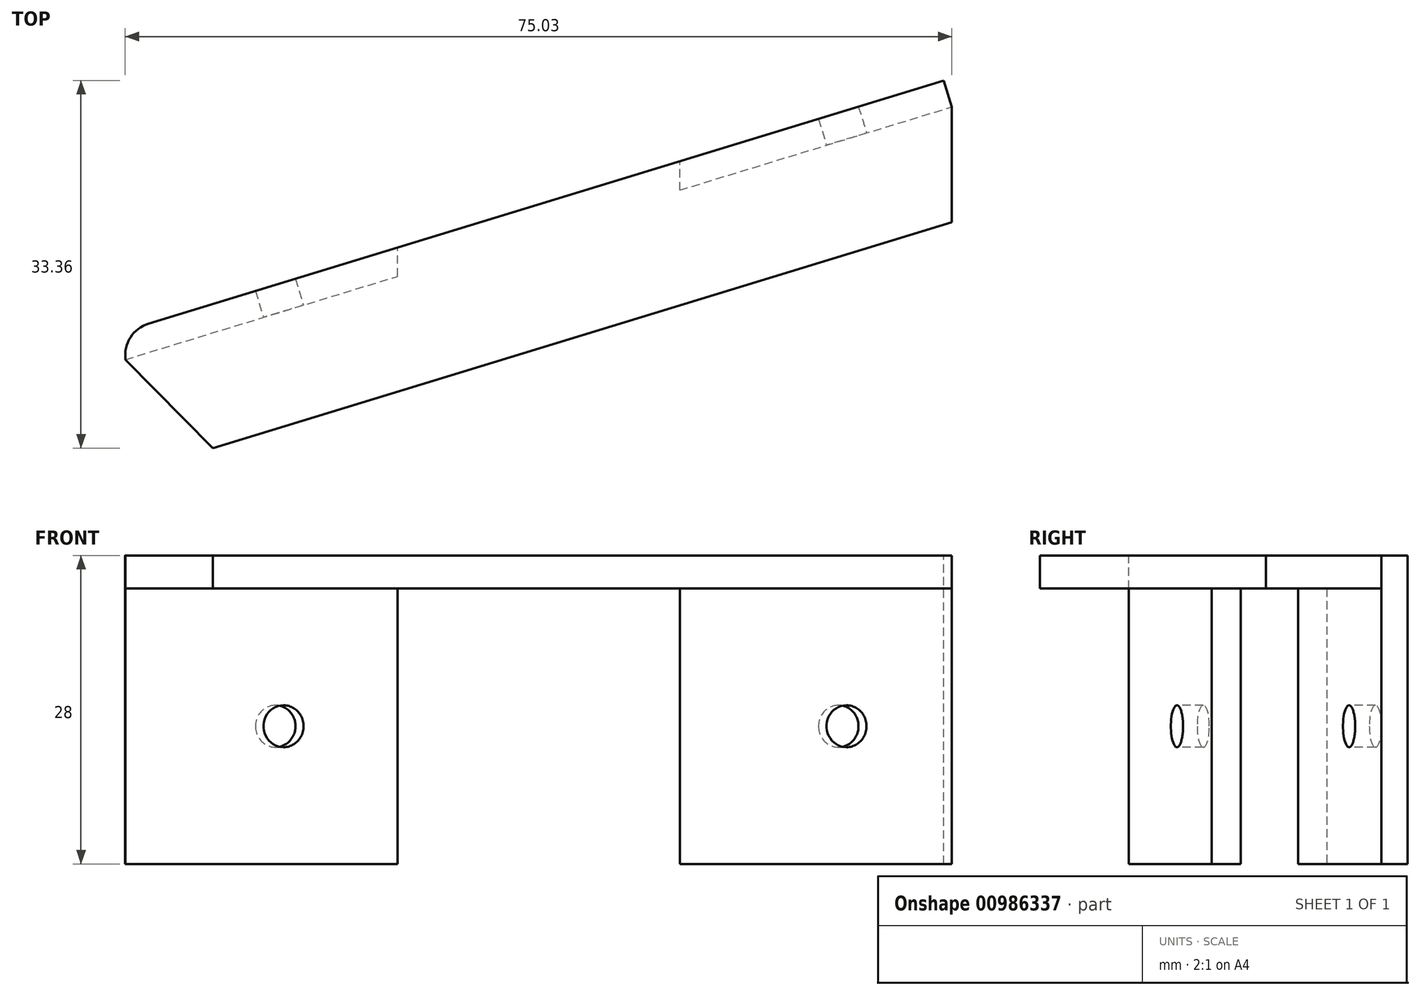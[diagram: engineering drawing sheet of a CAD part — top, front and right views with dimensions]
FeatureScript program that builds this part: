
annotation { "Feature Type Name" : "Feature", "Feature Type Description" : "" }
export const myFeature = defineFeature(function(context is Context, id is Id, definition is map)
    precondition{}
    {
        {
            var Q0;
            Q0=qCreatedBy(makeId("Top.planeOp"),FACE);
            var sketch = newSketch(context, id + "F0", { "sketchPlane" : qUnion([Q0])});
            skLineSegment(sketch, "E0.bottom", {"start": v(0, 0) * mm, "end": v(50, 0) * mm});
            skLineSegment(sketch, "E0.top", {"start": v(0, 33) * mm, "end": v(50, 33) * mm});
            skLineSegment(sketch, "E0.left", {"start": v(0, 0) * mm, "end": v(0, 33) * mm});
            skLineSegment(sketch, "E0.right", {"start": v(50, 0) * mm, "end": v(50, 33) * mm});
            skLineSegment(sketch, "E1", {"start": v(0, 33) * mm, "end": v(50, 48.29) * mm});
            skLineSegment(sketch, "E2", {"start": v(50, 33) * mm, "end": v(50, 48.29) * mm});
            skLineSegment(sketch, "E3", {"start": v(0, 33) * mm, "end": v(-25, 25.36) * mm});
            skLineSegment(sketch, "E4", {"start": v(-25, 25.36) * mm, "end": v(0, 0) * mm});
            skLineSegment(sketch, "E5", {"start": v(0, 33) * mm, "end": v(0, 137) * mm});
            skLineSegment(sketch, "E6", {"start": v(0, 137) * mm, "end": v(25, 137) * mm});
            skLineSegment(sketch, "E7", {"start": v(25, 137) * mm, "end": v(25, 0) * mm});
            skLineSegment(sketch, "E8", {"start": v(0, 137) * mm, "end": v(-25, 131.69) * mm});
            skLineSegment(sketch, "E9", {"start": v(-25, 131.69) * mm, "end": v(-25, 92.43) * mm});
            skLineSegment(sketch, "E10", {"start": v(-25, 131.69) * mm, "end": v(0, 101.46) * mm});
            skLineSegment(sketch, "E11", {"start": v(0, 137) * mm, "end": v(50, 147.63) * mm});
            skLineSegment(sketch, "E12", {"start": v(50, 147.63) * mm, "end": v(50, 131.69) * mm});
            skLineSegment(sketch, "E13", {"start": v(25, 101.46) * mm, "end": v(50, 131.69) * mm});
            skLineSegment(sketch, "E14", {"start": v(0, 137) * mm, "end": v(0, 177) * mm});
            skLineSegment(sketch, "E15", {"start": v(0, 177) * mm, "end": v(25, 177) * mm});
            skPoint(sketch, "E15.endSnap0", {"position": v(25, 142.31) * mm});
            skLineSegment(sketch, "E16", {"start": v(25, 177) * mm, "end": v(25, 137) * mm});
            skSolve(sketch);
        }
        {
            var Q0;
            Q0=qSketchRegion(id+"F0",true);
            extrude(context, id + "F1", {"entities" : qUnion([Q0]), "depth" : 25 * mm});
        }
        {
            var Q0;
            Q0=makeQuery(id+"F1.opExtrude","CAP_FACE",FACE,{"disambiguationData":[OSD([sQuery(id+"F0.wireOp",EDGE,"E0.bottom"),sQuery(id+"F0.wireOp",EDGE,"E0.right"),sQuery(id+"F0.wireOp",EDGE,"E1"),sQuery(id+"F0.wireOp",EDGE,"E2"),sQuery(id+"F0.wireOp",EDGE,"E3"),sQuery(id+"F0.wireOp",EDGE,"E4"),sQuery(id+"F0.wireOp",EDGE,"E5"),sQuery(id+"F0.wireOp",EDGE,"E7"),sQuery(id+"F0.wireOp",EDGE,"E8"),sQuery(id+"F0.wireOp",EDGE,"E10"),sQuery(id+"F0.wireOp",EDGE,"E11"),sQuery(id+"F0.wireOp",EDGE,"E12"),sQuery(id+"F0.wireOp",EDGE,"E13"),sQuery(id+"F0.wireOp",EDGE,"E14"),sQuery(id+"F0.wireOp",EDGE,"E15"),sQuery(id+"F0.wireOp",EDGE,"E16")])],"isStart":true});
            var sketch = newSketch(context, id + "F2", { "sketchPlane" : qUnion([Q0])});
            skLineSegment(sketch, "E17", {"start": v(25, -101.46) * mm, "end": v(0, -101.46) * mm});
            skLineSegment(sketch, "E18", {"start": v(0, -101.46) * mm, "end": v(-25, -131.69) * mm});
            skLineSegment(sketch, "E19", {"start": v(-25, -131.69) * mm, "end": v(50, -147.63) * mm});
            skLineSegment(sketch, "E20", {"start": v(50, -147.63) * mm, "end": v(50, -131.69) * mm});
            skLineSegment(sketch, "E21", {"start": v(50, -131.69) * mm, "end": v(25, -101.46) * mm});
            skSolve(sketch);
        }
        {
            var Q0;
            Q0=qSketchRegion(id+"F2",true);
            extrude(context, id + "F3", {"entities" : qUnion([Q0]), "operationType" : NewBodyOperationType.ADD, "depth" : 10 * mm});
        }
        {
            var Q0;
            Q0=makeQuery(id+"F1.opExtrude","SWEPT_FACE",FACE,{"disambiguationData":[OSD([sQuery(id+"F0.wireOp",EDGE,"E7")])]});
            var sketch = newSketch(context, id + "F4", { "sketchPlane" : qUnion([Q0])});
            skLineSegment(sketch, "E22", {"start": v(147.63, -10) * mm, "end": v(101.46, 0) * mm});
            skLineSegment(sketch, "E23", {"start": v(101.46, 0) * mm, "end": v(101.46, -21.14) * mm});
            skLineSegment(sketch, "E24", {"start": v(101.46, -21.14) * mm, "end": v(147.63, -10) * mm});
            skSolve(sketch);
        }
        {
            var Q0;
            Q0=qSketchRegion(id+"F4",true);
            extrude(context, id + "F5", {"entities" : qUnion([Q0]), "operationType" : NewBodyOperationType.REMOVE, "oppositeDirection" : true, "depth" : 163.4 * mm, "symmetric" : true});
        }
        {
            var Q0;
            {var subQ0=sQuery(id+"F0.wireOp",EDGE,"E13");var subQ1=sQuery(id+"F0.wireOp",EDGE,"E7");var subQ2=sQuery(id+"F0.wireOp",EDGE,"E5");var subQ3=sQuery(id+"F0.wireOp",EDGE,"E4");var subQ4=sQuery(id+"F0.wireOp",EDGE,"E0.bottom");var subQ5=sQuery(id+"F0.wireOp",EDGE,"E10");var subQ6=sQuery(id+"F0.wireOp",EDGE,"E2");var subQ7=sQuery(id+"F0.wireOp",EDGE,"E0.right");var subQ8=sQuery(id+"F0.wireOp",EDGE,"E1");var subQ9=sQuery(id+"F0.wireOp",EDGE,"E3");Q0=makeQuery(id+"F3.boolean.opBoolean","SPLIT",FACE,{"disambiguationData":[TD([makeQuery(id+"F1.opExtrude","SWEPT_FACE",FACE,{"disambiguationData":[OSD([subQ4])]})])],"derivedFrom":makeQuery(id+"F1.opExtrude","CAP_FACE",FACE,{"disambiguationData":[OSD([subQ4,subQ7,subQ8,subQ6,subQ9,subQ3,subQ2,subQ1,sQuery(id+"F0.wireOp",EDGE,"E8"),subQ5,sQuery(id+"F0.wireOp",EDGE,"E11"),sQuery(id+"F0.wireOp",EDGE,"E12"),subQ0,sQuery(id+"F0.wireOp",EDGE,"E14"),sQuery(id+"F0.wireOp",EDGE,"E15"),sQuery(id+"F0.wireOp",EDGE,"E16")])],"isStart":true})});}
            var sketch = newSketch(context, id + "F6", { "sketchPlane" : qUnion([Q0])});
            skLineSegment(sketch, "E25", {"start": v(50, 0) * mm, "end": v(50, -48.29) * mm});
            skLineSegment(sketch, "E26", {"start": v(50, -48.29) * mm, "end": v(-25, -25.36) * mm});
            skLineSegment(sketch, "E27", {"start": v(-25, -25.36) * mm, "end": v(0, 0) * mm});
            skLineSegment(sketch, "E28", {"start": v(0, 0) * mm, "end": v(50, 0) * mm});
            skSolve(sketch);
        }
        {
            var Q0;
            Q0=qSketchRegion(id+"F6",true);
            extrude(context, id + "F7", {"entities" : qUnion([Q0]), "operationType" : NewBodyOperationType.ADD, "depth" : 10 * mm});
        }
        {
            var Q0;
            Q0=makeQuery(id+"F7.boolean.opBoolean","MERGE",FACE,{"derivedFrom":[makeQuery(id+"F1.opExtrude","SWEPT_FACE",FACE,{"disambiguationData":[OSD([sQuery(id+"F0.wireOp",EDGE,"E0.right"),sQuery(id+"F0.wireOp",EDGE,"E2")])]}),makeQuery(id+"F7.opExtrude","SWEPT_FACE",FACE,{"disambiguationData":[OSD([sQuery(id+"F6.wireOp",EDGE,"E25")])]})]});
            var sketch = newSketch(context, id + "F8", { "sketchPlane" : qUnion([Q0])});
            skLineSegment(sketch, "E29", {"start": v(0, 0) * mm, "end": v(48.29, -10) * mm});
            skLineSegment(sketch, "E30", {"start": v(48.29, -10) * mm, "end": v(48.29, -39.53) * mm});
            skLineSegment(sketch, "E31", {"start": v(48.29, -39.53) * mm, "end": v(0, -39.53) * mm});
            skLineSegment(sketch, "E32", {"start": v(0, -39.53) * mm, "end": v(0, 0) * mm});
            skSolve(sketch);
        }
        {
            var Q0;
            Q0=qSketchRegion(id+"F8",true);
            extrude(context, id + "F9", {"entities" : qUnion([Q0]), "operationType" : NewBodyOperationType.REMOVE, "oppositeDirection" : true, "depth" : 92 * mm});
        }
        {
            var Q0;
            Q0=makeQuery(id+"F1.opExtrude","SWEPT_FACE",FACE,{"disambiguationData":[OSD([sQuery(id+"F0.wireOp",EDGE,"E15")])]});
            var sketch = newSketch(context, id + "F10", { "sketchPlane" : qUnion([Q0])});
            skLineSegment(sketch, "E33.bottom", {"start": v(-6, 19) * mm, "end": v(-19, 19) * mm});
            skLineSegment(sketch, "E33.top", {"start": v(-6, 6) * mm, "end": v(-19, 6) * mm});
            skLineSegment(sketch, "E33.left", {"start": v(-6, 19) * mm, "end": v(-6, 6) * mm});
            skLineSegment(sketch, "E33.right", {"start": v(-19, 19) * mm, "end": v(-19, 6) * mm});
            skPoint(sketch, "E33.middle", {"position": v(-12.5, 12.5) * mm});
            skPoint(sketch, "E33.middle.positionSnap0", {"position": v(-25, 12.5) * mm});
            skPoint(sketch, "E33.middle.positionSnap1", {"position": v(-12.5, 25) * mm});
            skPoint(sketch, "E33.centerSnap0", {"position": v(-25, 12.5) * mm});
            skPoint(sketch, "E33.centerSnap1", {"position": v(-12.5, 25) * mm});
            skSolve(sketch);
        }
        {
            var Q0;
            Q0=qSketchRegion(id+"F10",true);
            extrude(context, id + "F11", {"entities" : qUnion([Q0]), "operationType" : NewBodyOperationType.REMOVE, "oppositeDirection" : true, "depth" : 40 * mm});
        }
        {
            var Q0;
            Q0=makeQuery(id+"F3.boolean.opBoolean","MERGE",FACE,{"derivedFrom":[makeQuery(id+"F1.opExtrude","SWEPT_FACE",FACE,{"disambiguationData":[OSD([sQuery(id+"F0.wireOp",EDGE,"E8")])]}),makeQuery(id+"F1.opExtrude","SWEPT_FACE",FACE,{"disambiguationData":[OSD([sQuery(id+"F0.wireOp",EDGE,"E11")])]}),makeQuery(id+"F3.opExtrude","SWEPT_FACE",FACE,{"disambiguationData":[OSD([sQuery(id+"F2.wireOp",EDGE,"E19")])]})]});
            var sketch = newSketch(context, id + "F12", { "sketchPlane" : qUnion([Q0])});
            skLineSegment(sketch, "E34", {"start": v(-2.93, 25) * mm, "end": v(-2.93, 12.5) * mm});
            skPoint(sketch, "E34.endSnap0", {"position": v(-28.48, 12.5) * mm});
            skLineSegment(sketch, "E35", {"start": v(-2.93, 12.5) * mm, "end": v(-18.63, 12.5) * mm});
            skCircle(sketch, "E36", {"center": v(-18.63, 12.5) * mm, "radius": 1.9 * mm});
            skLineSegment(sketch, "E37", {"start": v(-79.6, 25) * mm, "end": v(-79.6, 12.5) * mm});
            skLineSegment(sketch, "E38", {"start": v(-79.6, 12.5) * mm, "end": v(-70.3, 12.5) * mm});
            skCircle(sketch, "E39", {"center": v(-70.3, 12.5) * mm, "radius": 1.9 * mm});
            skSolve(sketch);
        }
        {
            var Q0;
            Q0=qSketchRegion(id+"F12",true);
            extrude(context, id + "F13", {"entities" : qUnion([Q0]), "operationType" : NewBodyOperationType.REMOVE, "oppositeDirection" : true, "depth" : 7 * mm});
        }
        {
            var Q0;
            Q0=makeQuery(id+"F7.boolean.opBoolean","MERGE",FACE,{"derivedFrom":[makeQuery(id+"F1.opExtrude","SWEPT_FACE",FACE,{"disambiguationData":[OSD([sQuery(id+"F0.wireOp",EDGE,"E1")])]}),makeQuery(id+"F1.opExtrude","SWEPT_FACE",FACE,{"disambiguationData":[OSD([sQuery(id+"F0.wireOp",EDGE,"E3")])]}),makeQuery(id+"F7.opExtrude","SWEPT_FACE",FACE,{"disambiguationData":[OSD([sQuery(id+"F6.wireOp",EDGE,"E26")])]})]});
            cPlane(context, id + "F14", {"entities" : qUnion([Q0]), "cplaneType" : CPlaneType.OFFSET, "offset" : 0 * mm, "width" : 150 * mm, "height" : 150 * mm});
        }
        {
            var Q0;
            Q0=makeQuery(id+"F7.boolean.opBoolean","MERGE",FACE,{"derivedFrom":[makeQuery(id+"F1.opExtrude","SWEPT_FACE",FACE,{"disambiguationData":[OSD([sQuery(id+"F0.wireOp",EDGE,"E1")])]}),makeQuery(id+"F1.opExtrude","SWEPT_FACE",FACE,{"disambiguationData":[OSD([sQuery(id+"F0.wireOp",EDGE,"E3")])]}),makeQuery(id+"F7.opExtrude","SWEPT_FACE",FACE,{"disambiguationData":[OSD([sQuery(id+"F6.wireOp",EDGE,"E26")])]})]});
            extrude(context, id + "F15", {"entities" : qUnion([Q0]), "operationType" : NewBodyOperationType.ADD, "depth" : 2.5 * mm});
        }
        {
            var Q0;
            Q0=makeQuery(id+"F15.opExtrude","CAP_FACE",FACE,{"disambiguationData":[OSD([sQuery(id+"F0.wireOp",EDGE,"E1"),sQuery(id+"F0.wireOp",EDGE,"E3"),sQuery(id+"F6.wireOp",EDGE,"E26")])],"isStart":false});
            var sketch = newSketch(context, id + "F16", { "sketchPlane" : qUnion([Q0])});
            skLineSegment(sketch, "E40.bottom", {"start": v(16.5, 25) * mm, "end": v(-61.93, 25) * mm});
            skLineSegment(sketch, "E40.top", {"start": v(16.5, 0) * mm, "end": v(-61.93, 0) * mm});
            skLineSegment(sketch, "E40.left", {"start": v(16.5, 25) * mm, "end": v(16.5, 0) * mm});
            skLineSegment(sketch, "E40.right", {"start": v(-61.93, 25) * mm, "end": v(-61.93, 0) * mm});
            skSolve(sketch);
        }
        {
            var Q0;
            Q0=qSketchRegion(id+"F16",true);
            extrude(context, id + "F17", {"entities" : qUnion([Q0]), "operationType" : NewBodyOperationType.ADD, "oppositeDirection" : true, "depth" : 2.5 * mm});
        }
        {
            var Q0;
            Q0=makeQuery(id+"F17.boolean.opBoolean","MERGE",FACE,{"derivedFrom":[makeQuery(id+"F15.opExtrude","CAP_FACE",FACE,{"disambiguationData":[OSD([sQuery(id+"F0.wireOp",EDGE,"E1"),sQuery(id+"F0.wireOp",EDGE,"E3"),sQuery(id+"F6.wireOp",EDGE,"E26")])],"isStart":false}),makeQuery(id+"F17.opExtrude","CAP_FACE",FACE,{"disambiguationData":[OSD([sQuery(id+"F16.wireOp",EDGE,"E40.bottom"),sQuery(id+"F16.wireOp",EDGE,"E40.top"),sQuery(id+"F16.wireOp",EDGE,"E40.left"),sQuery(id+"F16.wireOp",EDGE,"E40.right")])],"isStart":true})]});
            var sketch = newSketch(context, id + "F18", { "sketchPlane" : qUnion([Q0])});
            skLineSegment(sketch, "E41.top", {"start": v(16.5, -3) * mm, "end": v(-61.93, -3) * mm});
            skLineSegment(sketch, "E42.bottom", {"start": v(16.5, -3) * mm, "end": v(-74.36, -3) * mm});
            skLineSegment(sketch, "E42.top", {"start": v(16.5, -15.71) * mm, "end": v(-74.36, -15.71) * mm});
            skLineSegment(sketch, "E42.left", {"start": v(16.5, -3) * mm, "end": v(16.5, -15.71) * mm});
            skLineSegment(sketch, "E42.right", {"start": v(-74.36, -3) * mm, "end": v(-74.36, -15.71) * mm});
            skSolve(sketch);
        }
        {
            var Q0;
            Q0=qSketchRegion(id+"F18",true);
            extrude(context, id + "F19", {"entities" : qUnion([Q0]), "operationType" : NewBodyOperationType.REMOVE, "oppositeDirection" : true, "depth" : 336 * mm});
        }
        {
            var Q0;
            {var subQ0=sQuery(id+"F0.wireOp",EDGE,"E3");var subQ1=sQuery(id+"F0.wireOp",EDGE,"E1");Q0=makeQuery(id+"F17.boolean.opBoolean","MERGE",FACE,{"derivedFrom":[makeQuery(id+"F15.boolean.opBoolean","MERGE",FACE,{"derivedFrom":[makeQuery(id+"F1.opExtrude","CAP_FACE",FACE,{"disambiguationData":[OSD([sQuery(id+"F0.wireOp",EDGE,"E0.bottom"),sQuery(id+"F0.wireOp",EDGE,"E0.right"),subQ1,sQuery(id+"F0.wireOp",EDGE,"E2"),subQ0,sQuery(id+"F0.wireOp",EDGE,"E4"),sQuery(id+"F0.wireOp",EDGE,"E5"),sQuery(id+"F0.wireOp",EDGE,"E7"),sQuery(id+"F0.wireOp",EDGE,"E8"),sQuery(id+"F0.wireOp",EDGE,"E10"),sQuery(id+"F0.wireOp",EDGE,"E11"),sQuery(id+"F0.wireOp",EDGE,"E12"),sQuery(id+"F0.wireOp",EDGE,"E13"),sQuery(id+"F0.wireOp",EDGE,"E14"),sQuery(id+"F0.wireOp",EDGE,"E15"),sQuery(id+"F0.wireOp",EDGE,"E16")])],"isStart":false}),makeQuery(id+"F15.opExtrude","SWEPT_FACE",FACE,{"disambiguationData":[OSD([subQ1])]}),makeQuery(id+"F15.opExtrude","SWEPT_FACE",FACE,{"disambiguationData":[OSD([subQ0])]})]}),makeQuery(id+"F17.opExtrude","SWEPT_FACE",FACE,{"disambiguationData":[OSD([sQuery(id+"F16.wireOp",EDGE,"E40.bottom")])]})]});}
            var sketch = newSketch(context, id + "F20", { "sketchPlane" : qUnion([Q0])});
            skLineSegment(sketch, "E43", {"start": v(-25, 25.36) * mm, "end": v(50, 48.29) * mm});
            skLineSegment(sketch, "E44", {"start": v(50, 48.29) * mm, "end": v(63.77, -9.77) * mm});
            skLineSegment(sketch, "E45", {"start": v(63.77, -9.77) * mm, "end": v(-20.6, -5.85) * mm});
            skLineSegment(sketch, "E46", {"start": v(-20.6, -5.85) * mm, "end": v(-25, 25.36) * mm});
            skSolve(sketch);
        }
        {
            var Q0;
            Q0=qSketchRegion(id+"F20",true);
            extrude(context, id + "F21", {"entities" : qUnion([Q0]), "operationType" : NewBodyOperationType.REMOVE, "oppositeDirection" : true, "depth" : 25 * mm});
        }
        {
            var Q0;
            Q0=qCreatedBy(id+"F14.planeOp",FACE);
            cPlane(context, id + "F22", {"entities" : qUnion([Q0]), "cplaneType" : CPlaneType.OFFSET, "offset" : 10 * mm, "oppositeDirection" : true, "width" : 150 * mm, "height" : 150 * mm});
        }
        {
            var Q0;
            Q0=qCreatedBy(id+"F22.planeOp",FACE);
            var sketch = newSketch(context, id + "F23", { "sketchPlane" : qUnion([Q0])});
            skLineSegment(sketch, "E47.bottom", {"start": v(-66.06, 2.6) * mm, "end": v(24.9, 2.6) * mm});
            skLineSegment(sketch, "E47.top", {"start": v(-66.06, -7.75) * mm, "end": v(24.9, -7.75) * mm});
            skLineSegment(sketch, "E47.left", {"start": v(-66.06, 2.6) * mm, "end": v(-66.06, -7.75) * mm});
            skLineSegment(sketch, "E47.right", {"start": v(24.9, 2.6) * mm, "end": v(24.9, -7.75) * mm});
            skSolve(sketch);
        }
        {
            var Q0;
            Q0=qSketchRegion(id+"F23",true);
            extrude(context, id + "F24", {"entities" : qUnion([Q0]), "operationType" : NewBodyOperationType.REMOVE, "oppositeDirection" : true, "depth" : 48.1 * mm});
        }
        {
            var Q0;
            Q0=makeQuery(id+"F1.opExtrude","SWEPT_FACE",FACE,{"disambiguationData":[OSD([sQuery(id+"F0.wireOp",EDGE,"E15")])]});
            var sketch = newSketch(context, id + "F25", { "sketchPlane" : qUnion([Q0])});
            skLineSegment(sketch, "E48.bottom", {"start": v(0, 25) * mm, "end": v(-25, 25) * mm});
            skLineSegment(sketch, "E48.top", {"start": v(0, 0) * mm, "end": v(-25, 0) * mm});
            skLineSegment(sketch, "E49.bottom", {"start": v(-25, 0) * mm, "end": v(-25.3, 0) * mm});
            skLineSegment(sketch, "E49.top", {"start": v(-25, 25) * mm, "end": v(-25.3, 25) * mm});
            skLineSegment(sketch, "E49.right", {"start": v(-25.3, 0) * mm, "end": v(-25.3, 25) * mm});
            skLineSegment(sketch, "E50.bottom", {"start": v(0, 25) * mm, "end": v(0.3, 25) * mm});
            skLineSegment(sketch, "E50.top", {"start": v(0, 0) * mm, "end": v(0.3, 0) * mm});
            skLineSegment(sketch, "E50.right", {"start": v(0.3, 25) * mm, "end": v(0.3, 0) * mm});
            skSolve(sketch);
        }
        {
            var Q0;
            Q0=qSketchRegion(id+"F25",true);
            extrude(context, id + "F26", {"entities" : qUnion([Q0]), "operationType" : NewBodyOperationType.REMOVE, "oppositeDirection" : true, "depth" : 199 * mm});
        }
        {
            var Q0;
            Q0=makeQuery(id+"F17.boolean.opBoolean","MERGE",FACE,{"derivedFrom":[makeQuery(id+"F15.opExtrude","CAP_FACE",FACE,{"disambiguationData":[OSD([sQuery(id+"F0.wireOp",EDGE,"E1"),sQuery(id+"F0.wireOp",EDGE,"E3"),sQuery(id+"F6.wireOp",EDGE,"E26")])],"isStart":false}),makeQuery(id+"F17.opExtrude","CAP_FACE",FACE,{"disambiguationData":[OSD([sQuery(id+"F16.wireOp",EDGE,"E40.bottom"),sQuery(id+"F16.wireOp",EDGE,"E40.top"),sQuery(id+"F16.wireOp",EDGE,"E40.left"),sQuery(id+"F16.wireOp",EDGE,"E40.right")])],"isStart":true})]});
            var sketch = newSketch(context, id + "F27", { "sketchPlane" : qUnion([Q0])});
            skLineSegment(sketch, "E51.bottom", {"start": v(40.08, -30.15) * mm, "end": v(-143.24, -30.15) * mm});
            skLineSegment(sketch, "E51.top", {"start": v(40.08, 53.76) * mm, "end": v(-143.24, 53.76) * mm});
            skLineSegment(sketch, "E51.left", {"start": v(40.08, -30.15) * mm, "end": v(40.08, 53.76) * mm});
            skLineSegment(sketch, "E51.right", {"start": v(-143.24, -30.15) * mm, "end": v(-143.24, 53.76) * mm});
            skSolve(sketch);
        }
        {
            var Q0;
            Q0=qSketchRegion(id+"F27",true);
            extrude(context, id + "F28", {"entities" : qUnion([Q0]), "operationType" : NewBodyOperationType.REMOVE, "depth" : 179 * mm});
        }
        {
            var Q0;
            Q0=makeQuery(id+"F15.opExtrude","CAP_EDGE",EDGE,{"disambiguationData":[OSD([sQuery(id+"F0.wireOp",EDGE,"E3"),sQuery(id+"F0.wireOp",EDGE,"E4"),sQuery(id+"F6.wireOp",EDGE,"E26"),sQuery(id+"F6.wireOp",EDGE,"E27")])],"isStart":false});
            fillet(context, id + "F29", {"entities" : qUnion([Q0]), "radius" : 3 * mm, "tangentPropagation" : true, "allowEdgeOverflow" : false});
        }
        {
            var Q0;
            {var subQ2=sQuery(id+"F0.wireOp",EDGE,"E4");var subQ4=sQuery(id+"F20.wireOp",EDGE,"E43");Q0=makeQuery(id+"F26.boolean.opBoolean","SPLIT",FACE,{"disambiguationData":[TD([makeQuery(id+"F1.opExtrude","SWEPT_FACE",FACE,{"disambiguationData":[OSD([subQ2])]})])],"derivedFrom":makeQuery(id+"F21.boolean.opBoolean","COPY",FACE,{"derivedFrom":makeQuery(id+"F21.opExtrude","SWEPT_FACE",FACE,{"disambiguationData":[OSD([subQ4])]})})});}
            var sketch = newSketch(context, id + "F30", { "sketchPlane" : qUnion([Q0])});
            skLineSegment(sketch, "E52", {"start": v(-16.5, 25) * mm, "end": v(-16.5, 12.5) * mm});
            skLineSegment(sketch, "E53", {"start": v(-16.5, 12.5) * mm, "end": v(-1.5, 12.5) * mm});
            skCircle(sketch, "E54", {"center": v(-1.5, 12.5) * mm, "radius": 1.9 * mm});
            skSolve(sketch);
        }
        {
            var Q0;
            Q0=qSketchRegion(id+"F30",true);
            extrude(context, id + "F31", {"entities" : qUnion([Q0]), "operationType" : NewBodyOperationType.REMOVE, "oppositeDirection" : true, "depth" : 25 * mm});
        }
        {
            var Q0;
            {var subQ3=sQuery(id+"F6.wireOp",EDGE,"E25");var subQ5=sQuery(id+"F20.wireOp",EDGE,"E43");Q0=makeQuery(id+"F26.boolean.opBoolean","SPLIT",FACE,{"disambiguationData":[TD([makeQuery(id+"F7.opExtrude","SWEPT_FACE",FACE,{"disambiguationData":[OSD([subQ3])]})])],"derivedFrom":makeQuery(id+"F21.boolean.opBoolean","COPY",FACE,{"derivedFrom":makeQuery(id+"F21.opExtrude","SWEPT_FACE",FACE,{"disambiguationData":[OSD([subQ5])]})})});}
            var sketch = newSketch(context, id + "F32", { "sketchPlane" : qUnion([Q0])});
            skLineSegment(sketch, "E55", {"start": v(61.93, 25) * mm, "end": v(61.93, 12.5) * mm});
            skLineSegment(sketch, "E56", {"start": v(61.93, 12.5) * mm, "end": v(51.93, 12.5) * mm});
            skCircle(sketch, "E57", {"center": v(51.93, 12.5) * mm, "radius": 1.9 * mm});
            skSolve(sketch);
        }
        {
            var Q0;
            Q0=qSketchRegion(id+"F32",true);
            extrude(context, id + "F33", {"entities" : qUnion([Q0]), "operationType" : NewBodyOperationType.REMOVE, "oppositeDirection" : true, "depth" : 25 * mm});
        }
        {
            var Q0;
            Q0=makeQuery(id+"F19.boolean.opBoolean","COPY",FACE,{"derivedFrom":makeQuery(id+"F19.opExtrude","SWEPT_FACE",FACE,{"disambiguationData":[OSD([sQuery(id+"F18.wireOp",EDGE,"E42.bottom")])]})});
            cPlane(context, id + "F34", {"entities" : qUnion([Q0]), "cplaneType" : CPlaneType.OFFSET, "offset" : 5 * mm, "width" : 150 * mm, "height" : 150 * mm});
        }
        {
            var Q0;
            Q0=makeQuery(id+"F26.boolean.opBoolean","SPLIT",BODY,{"disambiguationData":[OD(1.0)],"derivedFrom":makeQuery(id+"F1.opExtrude","SWEPT_BODY",BODY,{"disambiguationData":[OSD([sQuery(id+"F0.wireOp",EDGE,"E0.bottom"),sQuery(id+"F0.wireOp",EDGE,"E0.right"),sQuery(id+"F0.wireOp",EDGE,"E1"),sQuery(id+"F0.wireOp",EDGE,"E2"),sQuery(id+"F0.wireOp",EDGE,"E3"),sQuery(id+"F0.wireOp",EDGE,"E4"),sQuery(id+"F0.wireOp",EDGE,"E5"),sQuery(id+"F0.wireOp",EDGE,"E7"),sQuery(id+"F0.wireOp",EDGE,"E8"),sQuery(id+"F0.wireOp",EDGE,"E10"),sQuery(id+"F0.wireOp",EDGE,"E11"),sQuery(id+"F0.wireOp",EDGE,"E12"),sQuery(id+"F0.wireOp",EDGE,"E13"),sQuery(id+"F0.wireOp",EDGE,"E14"),sQuery(id+"F0.wireOp",EDGE,"E15"),sQuery(id+"F0.wireOp",EDGE,"E16")])]})});
            var Q1;
            Q1=qCreatedBy(id+"F34.planeOp",FACE);
            mirror(context, id + "F35", {"entities" : qUnion([Q0]), "mirrorPlane" : qUnion([Q1])});
        }
        {
            var Q0;
            Q0=qCreatedBy(id+"F34.planeOp",FACE);
            var sketch = newSketch(context, id + "F36", { "sketchPlane" : qUnion([Q0])});
            skLineSegment(sketch, "E58.bottom", {"start": v(-39.29, 3.32) * mm, "end": v(65.61, 3.32) * mm});
            skLineSegment(sketch, "E58.top", {"start": v(-39.29, -68.62) * mm, "end": v(65.61, -68.62) * mm});
            skLineSegment(sketch, "E58.left", {"start": v(-39.29, 3.32) * mm, "end": v(-39.29, -68.62) * mm});
            skLineSegment(sketch, "E58.right", {"start": v(65.61, 3.32) * mm, "end": v(65.61, -68.62) * mm});
            skSolve(sketch);
        }
        {
            var Q0;
            Q0=qSketchRegion(id+"F36",true);
            extrude(context, id + "F37", {"entities" : qUnion([Q0]), "operationType" : NewBodyOperationType.REMOVE, "oppositeDirection" : true, "depth" : 57.7 * mm});
        }
    });
